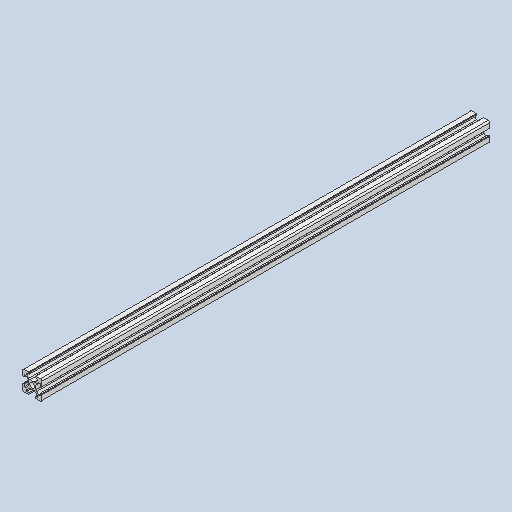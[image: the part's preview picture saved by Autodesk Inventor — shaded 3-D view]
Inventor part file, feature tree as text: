
AUTODESK INVENTOR PART (.ipt)
format: ipt  version: 2023 (Build 270158000, 158)  size: 256,512 bytes
history: native  units: mm
features: extrude x1, sketch x1, projected_geometry x1
ambient origin geometry x8: Origin, YZ Plane, XZ Plane, XY Plane, X Axis, Y Axis, Z Axis, Center Point
bodies: Solid1 (feature_tree), Body1 (feature_tree)
feature tree (3):
  extrude  "Extrusion1"  [1 undecoded]
  sketch  "Sketch1"  dims[d0=360.0mm d1=0.0mm]
  projected_geometry  "Projected Loop1"
note: 1 required parameter value undecoded (feature->parameter linkage not recoverable at this tier; creation-order binding heuristic only, values carry confidence <= 0.55)
